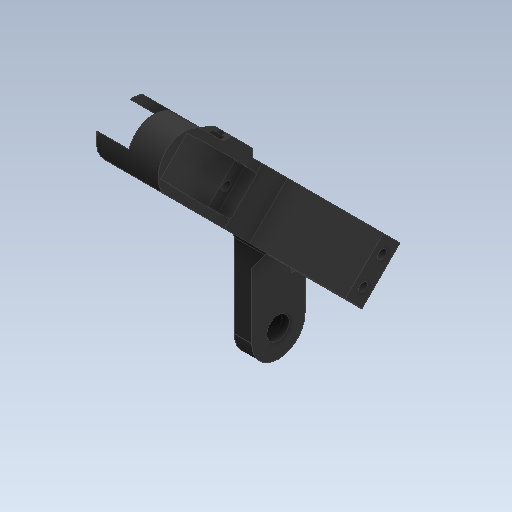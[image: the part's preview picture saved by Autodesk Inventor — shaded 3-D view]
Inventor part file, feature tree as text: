
AUTODESK INVENTOR PART (.ipt)
format: ipt  version: 2020 (Build 240168000, 168)  size: 580,608 bytes
history: native  units: in
note: dims shown in document units (in); Inventor stores cm internally (conversion verified against a paired STEP export)
features: sketch x26, other x8, extrude x5, projected_geometry x5, chamfer x4, plane x4
ambient origin geometry x8: Origin, YZ Plane, XZ Plane, XY Plane, X Axis, Y Axis, Z Axis, Center Point
bodies: Solid2 (feature_tree), Solid3 (feature_tree), Solid1 (feature_tree), Solid4 (feature_tree), Solid5 (feature_tree)
feature tree (52):
  other  "LegMidBot.ipt"
  chamfer  "Chamfer1"  Distance=0.0787in Angle=45.0deg
  chamfer  "Chamfer2"  Distance=0.0787in Angle=45.0deg
  chamfer  "Chamfer3"  Distance=0.1969in Angle=45.0deg
  chamfer  "Chamfer4"  Distance=0.0787in Angle=45.0deg
  extrude  "Extrusion4"  Depth=0.4813in TaperAngle=0.0deg
  extrude  "Extrusion5"  Depth=0.0059in
  extrude  "Extrusion6"  Depth=0.3937in TaperAngle=0.0deg
  extrude  "Extrusion7"  Depth=0.0039in
  extrude  "Extrusion8"  Depth=0.3937in TaperAngle=0.0deg
  other  "Solid1::LegMidBot.ipt"
  other  "Solid2::LegMidBot.ipt"
  other  "Solid3::LegMidBot.ipt"
  other  "Solid4::LegMidBot.ipt"
  other  "Solid5::LegMidBot.ipt"
  other  "Solid6::LegMidBot.ipt"
  other  "TaggingFeature1"
  sketch  "Sketch1"  dims[d0=0.3937in d12=0.0787in d13=0.0787in d14=45.0deg d15=0.0787in d16=0.0787in d17=45.0deg d18=0.1969in d19=0.0787in d20=45.0deg d21=0.0787in d22=0.0787in d23=45.0deg]
  sketch  "Sketch2"  dims[d24=0.1147in d25=0.4813in d26=0.0in]
  sketch  "Sketch3"  dims[d27=0.0059in d28=0.0059in]
  sketch  "Sketch4"  dims[d29=0.0059in d30=0.3937in d31=0.0in]
  sketch  "Sketch5"  dims[d32=0.0039in d33=0.0039in]
  sketch  "Sketch12"  dims[d34=0.3937in d35=0.0in d36=0.3937in d37=0.0in]
  sketch  "Sketch14"  dims[d38=0.3937in d39=0.0in]
  sketch  "Sketch15"
  sketch  "Sketch16"
  sketch  "Sketch17"
  sketch  "Sketch19"
  sketch  "Sketch22"
  sketch  "Sketch23"
  sketch  "Sketch25"
  sketch  "Sketch26"
  sketch  "Sketch27"
  sketch  "Sketch28"
  sketch  "Sketch32"
  sketch  "Sketch33"
  sketch  "Sketch39"
  sketch  "Sketch40"
  plane  "Work Plane1"
  plane  "Work Plane2"
  plane  "Work Plane3"
  plane  "Work Plane4"
  sketch  "Sketch46"
  projected_geometry  "Projected Loop5"
  sketch  "Sketch47"
  projected_geometry  "Projected Loop6"
  sketch  "Sketch48"
  projected_geometry  "Projected Loop7"
  sketch  "Sketch49"
  projected_geometry  "Projected Loop8"
  projected_geometry  "Projected Loop9"
  sketch  "Sketch50"
